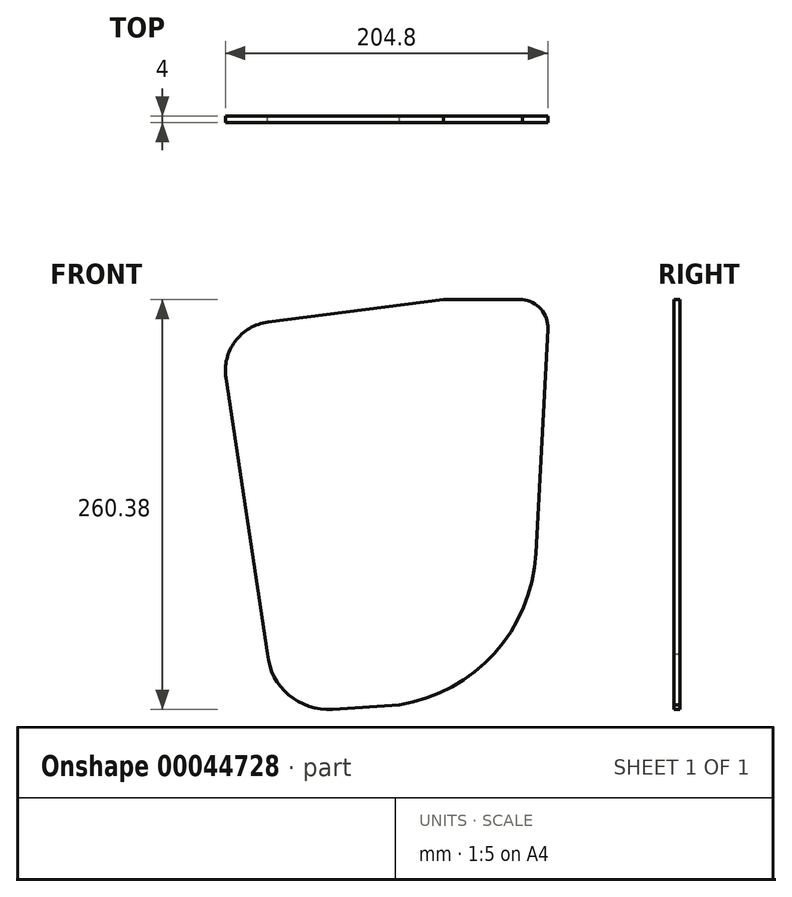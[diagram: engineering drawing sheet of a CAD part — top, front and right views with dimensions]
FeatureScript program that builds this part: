
annotation { "Feature Type Name" : "Feature", "Feature Type Description" : "" }
export const myFeature = defineFeature(function(context is Context, id is Id, definition is map)
    precondition{}
    {
        {
            var Q0;
            Q0=qCreatedBy(makeId("Front.planeOp"),FACE);
            var sketch = newSketch(context, id + "F0", { "sketchPlane" : qUnion([Q0])});
            skLineSegment(sketch, "E0.bottom", {"start": v(0, 0) * mm, "end": v(225, 0) * mm});
            skLineSegment(sketch, "E0.top", {"start": v(0, 275) * mm, "end": v(225, 275) * mm});
            skLineSegment(sketch, "E0.left", {"start": v(0, 0) * mm, "end": v(0, 275) * mm});
            skLineSegment(sketch, "E0.right", {"start": v(225, 0) * mm, "end": v(225, 275) * mm});
            skLineSegment(sketch, "E1", {"start": v(25, 275) * mm, "end": v(25, 0) * mm, "construction": true});
            skLineSegment(sketch, "E2.1.0.0", {"start": v(50, 275) * mm, "end": v(50, 0) * mm, "construction": true});
            skLineSegment(sketch, "E2.2.0.0", {"start": v(75, 275) * mm, "end": v(75, 0) * mm, "construction": true});
            skLineSegment(sketch, "E2.3.0.0", {"start": v(100, 275) * mm, "end": v(100, 0) * mm, "construction": true});
            skLineSegment(sketch, "E2.4.0.0", {"start": v(125, 275) * mm, "end": v(125, 0) * mm, "construction": true});
            skLineSegment(sketch, "E2.5.0.0", {"start": v(150, 275) * mm, "end": v(150, 0) * mm, "construction": true});
            skLineSegment(sketch, "E2.6.0.0", {"start": v(175, 275) * mm, "end": v(175, 0) * mm, "construction": true});
            skLineSegment(sketch, "E2.7.0.0", {"start": v(200, 275) * mm, "end": v(200, 0) * mm, "construction": true});
            skLineSegment(sketch, "E2.direction1", {"start": v(25, 0) * mm, "end": v(50, 0) * mm, "construction": true});
            skLineSegment(sketch, "E3", {"start": v(0, 25) * mm, "end": v(225, 25) * mm, "construction": true});
            skLineSegment(sketch, "E4", {"start": v(0, 50) * mm, "end": v(225, 50) * mm, "construction": true});
            skLineSegment(sketch, "E5", {"start": v(0, 75) * mm, "end": v(225, 75) * mm, "construction": true});
            skLineSegment(sketch, "E6", {"start": v(0, 100) * mm, "end": v(225, 100) * mm, "construction": true});
            skLineSegment(sketch, "E7", {"start": v(0, 125) * mm, "end": v(225, 125) * mm, "construction": true});
            skLineSegment(sketch, "E8.MirrorCS", {"start": v(0, 150) * mm, "end": v(225, 150) * mm, "construction": true});
            skLineSegment(sketch, "E9.MirrorCS", {"start": v(0, 175) * mm, "end": v(225, 175) * mm, "construction": true});
            skLineSegment(sketch, "E10.MirrorCS", {"start": v(0, 200) * mm, "end": v(225, 200) * mm, "construction": true});
            skLineSegment(sketch, "E11.MirrorCS", {"start": v(0, 225) * mm, "end": v(225, 225) * mm, "construction": true});
            skLineSegment(sketch, "E12.MirrorCS", {"start": v(0, 250) * mm, "end": v(225, 250) * mm, "construction": true});
            skSolve(sketch);
        }
        {
            var Q0;
            Q0=qCreatedBy(makeId("Front.planeOp"),FACE);
            var sketch = newSketch(context, id + "F1", { "sketchPlane" : qUnion([Q0])});
            skLineSegment(sketch, "E13", {"start": v(11.8, 225) * mm, "end": v(38.2, 50) * mm});
            skLineSegment(sketch, "E14", {"start": v(79.5, 14.7) * mm, "end": v(121.9, 17.5) * mm});
            skLineSegment(sketch, "E15", {"start": v(38.5, 260.6) * mm, "end": v(150, 275) * mm});
            skLineSegment(sketch, "E16", {"start": v(150, 275) * mm, "end": v(200, 275) * mm});
            skLineSegment(sketch, "E17", {"start": v(216.2, 256.2) * mm, "end": v(208.6, 113.7) * mm});
            skArc(sketch, "E18", {"start": v(38.5, 260.6) * mm, "mid": v(17.64, 248.44) * mm, "end": v(11.8, 225) * mm});
            skArc(sketch, "E19", {"start": v(38.2, 50) * mm, "mid": v(51.67, 23.94) * mm, "end": v(79.5, 14.7) * mm});
            skArc(sketch, "E20", {"start": v(121.9, 17.5) * mm, "mid": v(182.27, 50.26) * mm, "end": v(208.6, 113.7) * mm});
            skArc(sketch, "E21", {"start": v(216.2, 256.2) * mm, "mid": v(211.88, 268.86) * mm, "end": v(200, 275) * mm});
            skSolve(sketch);
        }
        {
            var Q0;
            Q0=qSketchRegion(id+"F1",true);
            extrude(context, id + "F2", {"entities" : qUnion([Q0]), "depth" : 2 * mm, "hasSecondDirection" : true, "secondDirectionOppositeDirection" : true, "secondDirectionDepth" : 2 * mm});
        }
    });
